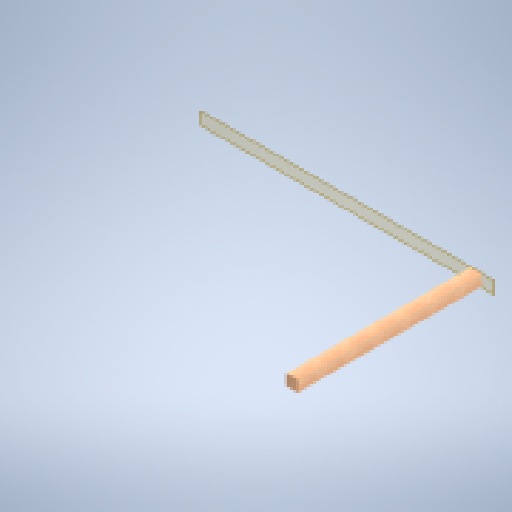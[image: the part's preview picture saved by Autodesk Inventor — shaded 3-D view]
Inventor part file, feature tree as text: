
AUTODESK INVENTOR PART (.ipt)
format: ipt  version: 2025 (Build 290162000, 162)  size: 138,752 bytes
history: native  units: in
note: dims shown in document units (in); Inventor stores cm internally (conversion verified against a paired STEP export)
features: plane x1, extrude x1, sketch x1
ambient origin geometry x8: Origin, YZ Plane, XZ Plane, XY Plane, X Axis, Y Axis, Z Axis, Center Point
bodies: Solid1 (feature_tree)
feature tree (3):
  plane  "Work Plane2"
  extrude  "Extrusion1"  Depth=4.0in
  sketch  "Sketch1"  dims[d0=4.0in d1=4.0in d2=66.0in d3=0.0in]
